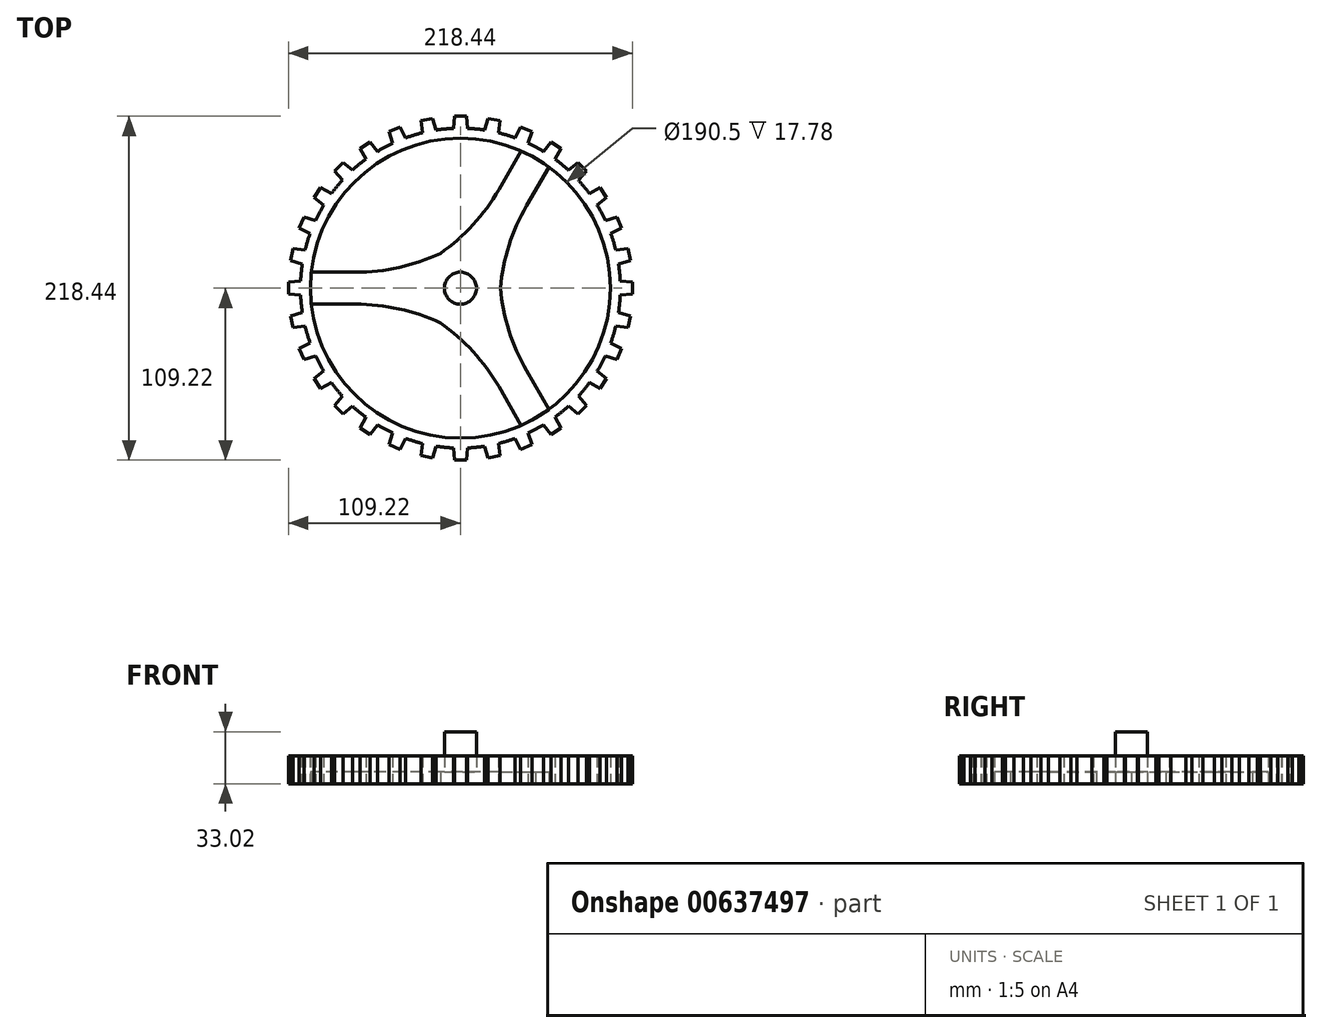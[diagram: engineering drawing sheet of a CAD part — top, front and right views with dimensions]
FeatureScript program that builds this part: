
annotation { "Feature Type Name" : "Feature", "Feature Type Description" : "" }
export const myFeature = defineFeature(function(context is Context, id is Id, definition is map)
    precondition{}
    {
        {
            var Q0;
            Q0=qCreatedBy(makeId("Top.planeOp"),FACE);
            var sketch = newSketch(context, id + "F0", { "sketchPlane" : qUnion([Q0])});
            skCircle(sketch, "E0", {"center": v(0, 0) * mm, "radius": 10.16 * mm});
            skCircle(sketch, "E1", {"center": v(0, 0) * mm, "radius": 12.7 * mm});
            skCircle(sketch, "E2", {"center": v(0, 0) * mm, "radius": 95.25 * mm});
            skCircle(sketch, "E3", {"center": v(0, 0) * mm, "radius": 101.6 * mm});
            skLineSegment(sketch, "E4", {"start": v(109.22, -3.81) * mm, "end": v(109.22, 3.81) * mm});
            skLineSegment(sketch, "E5", {"start": v(109.22, 3.81) * mm, "end": v(0, 12.7) * mm});
            skLineSegment(sketch, "E6", {"start": v(0, 12.7) * mm, "end": v(0, -12.7) * mm});
            skLineSegment(sketch, "E7", {"start": v(0, -12.7) * mm, "end": v(109.22, -3.81) * mm});
            skLineSegment(sketch, "E8", {"start": v(0, 0) * mm, "end": v(109.22, 0) * mm});
            skLineSegment(sketch, "E9.1.0", {"start": v(107.86, 17.57) * mm, "end": v(106.38, 25.04) * mm});
            skLineSegment(sketch, "E9.1.1", {"start": v(2.48, -12.46) * mm, "end": v(107.86, 17.57) * mm});
            skLineSegment(sketch, "E9.1.2", {"start": v(106.38, 25.04) * mm, "end": v(-2.48, 12.46) * mm});
            skLineSegment(sketch, "E9.2.0", {"start": v(102.36, 38.28) * mm, "end": v(99.45, 45.32) * mm});
            skLineSegment(sketch, "E9.2.1", {"start": v(4.86, -11.73) * mm, "end": v(102.36, 38.28) * mm});
            skLineSegment(sketch, "E9.2.2", {"start": v(99.45, 45.32) * mm, "end": v(-4.86, 11.73) * mm});
            skLineSegment(sketch, "E9.3.0", {"start": v(92.93, 57.51) * mm, "end": v(88.7, 63.85) * mm});
            skLineSegment(sketch, "E9.3.1", {"start": v(7.06, -10.56) * mm, "end": v(92.93, 57.51) * mm});
            skLineSegment(sketch, "E9.3.2", {"start": v(88.7, 63.85) * mm, "end": v(-7.06, 10.56) * mm});
            skLineSegment(sketch, "E9.4.0", {"start": v(79.92, 74.54) * mm, "end": v(74.54, 79.92) * mm});
            skLineSegment(sketch, "E9.4.1", {"start": v(8.98, -8.98) * mm, "end": v(79.92, 74.54) * mm});
            skLineSegment(sketch, "E9.4.2", {"start": v(74.54, 79.92) * mm, "end": v(-8.98, 8.98) * mm});
            skLineSegment(sketch, "E9.5.0", {"start": v(63.85, 88.7) * mm, "end": v(57.51, 92.93) * mm});
            skLineSegment(sketch, "E9.5.1", {"start": v(10.56, -7.06) * mm, "end": v(63.85, 88.7) * mm});
            skLineSegment(sketch, "E9.5.2", {"start": v(57.51, 92.93) * mm, "end": v(-10.56, 7.06) * mm});
            skLineSegment(sketch, "E9.6.0", {"start": v(45.32, 99.45) * mm, "end": v(38.28, 102.36) * mm});
            skLineSegment(sketch, "E9.6.1", {"start": v(11.73, -4.86) * mm, "end": v(45.32, 99.45) * mm});
            skLineSegment(sketch, "E9.6.2", {"start": v(38.28, 102.36) * mm, "end": v(-11.73, 4.86) * mm});
            skLineSegment(sketch, "E9.7.0", {"start": v(25.04, 106.38) * mm, "end": v(17.57, 107.86) * mm});
            skLineSegment(sketch, "E9.7.1", {"start": v(12.46, -2.48) * mm, "end": v(25.04, 106.38) * mm});
            skLineSegment(sketch, "E9.7.2", {"start": v(17.57, 107.86) * mm, "end": v(-12.46, 2.48) * mm});
            skLineSegment(sketch, "E9.8.0", {"start": v(3.81, 109.22) * mm, "end": v(-3.8, 109.22) * mm});
            skLineSegment(sketch, "E9.8.1", {"start": v(12.7, 0) * mm, "end": v(3.81, 109.22) * mm});
            skLineSegment(sketch, "E9.8.2", {"start": v(-3.8, 109.22) * mm, "end": v(-12.7, 0) * mm});
            skLineSegment(sketch, "E9.9.0", {"start": v(-17.57, 107.86) * mm, "end": v(-25.04, 106.38) * mm});
            skLineSegment(sketch, "E9.9.1", {"start": v(12.46, 2.48) * mm, "end": v(-17.57, 107.86) * mm});
            skLineSegment(sketch, "E9.9.2", {"start": v(-25.04, 106.38) * mm, "end": v(-12.46, -2.48) * mm});
            skLineSegment(sketch, "E9.10.0", {"start": v(-38.28, 102.36) * mm, "end": v(-45.32, 99.45) * mm});
            skLineSegment(sketch, "E9.10.1", {"start": v(11.73, 4.86) * mm, "end": v(-38.28, 102.36) * mm});
            skLineSegment(sketch, "E9.10.2", {"start": v(-45.32, 99.45) * mm, "end": v(-11.73, -4.86) * mm});
            skLineSegment(sketch, "E9.11.0", {"start": v(-57.51, 92.93) * mm, "end": v(-63.85, 88.7) * mm});
            skLineSegment(sketch, "E9.11.1", {"start": v(10.56, 7.06) * mm, "end": v(-57.51, 92.93) * mm});
            skLineSegment(sketch, "E9.11.2", {"start": v(-63.85, 88.7) * mm, "end": v(-10.56, -7.06) * mm});
            skLineSegment(sketch, "E9.12.0", {"start": v(-74.54, 79.92) * mm, "end": v(-79.92, 74.54) * mm});
            skLineSegment(sketch, "E9.12.1", {"start": v(8.98, 8.98) * mm, "end": v(-74.54, 79.92) * mm});
            skLineSegment(sketch, "E9.12.2", {"start": v(-79.92, 74.54) * mm, "end": v(-8.98, -8.98) * mm});
            skLineSegment(sketch, "E9.13.0", {"start": v(-88.7, 63.85) * mm, "end": v(-92.93, 57.51) * mm});
            skLineSegment(sketch, "E9.13.1", {"start": v(7.06, 10.56) * mm, "end": v(-88.7, 63.85) * mm});
            skLineSegment(sketch, "E9.13.2", {"start": v(-92.93, 57.51) * mm, "end": v(-7.06, -10.56) * mm});
            skLineSegment(sketch, "E9.14.0", {"start": v(-99.45, 45.32) * mm, "end": v(-102.36, 38.28) * mm});
            skLineSegment(sketch, "E9.14.1", {"start": v(4.86, 11.73) * mm, "end": v(-99.45, 45.32) * mm});
            skLineSegment(sketch, "E9.14.2", {"start": v(-102.36, 38.28) * mm, "end": v(-4.86, -11.73) * mm});
            skLineSegment(sketch, "E9.15.0", {"start": v(-106.38, 25.04) * mm, "end": v(-107.86, 17.57) * mm});
            skLineSegment(sketch, "E9.15.1", {"start": v(2.48, 12.46) * mm, "end": v(-106.38, 25.04) * mm});
            skLineSegment(sketch, "E9.15.2", {"start": v(-107.86, 17.57) * mm, "end": v(-2.48, -12.46) * mm});
            skLineSegment(sketch, "E9.16.0", {"start": v(-109.22, 3.81) * mm, "end": v(-109.22, -3.8) * mm});
            skLineSegment(sketch, "E9.16.1", {"start": v(0, 12.7) * mm, "end": v(-109.22, 3.81) * mm});
            skLineSegment(sketch, "E9.16.2", {"start": v(-109.22, -3.8) * mm, "end": v(0, -12.7) * mm});
            skLineSegment(sketch, "E9.17.0", {"start": v(-107.86, -17.57) * mm, "end": v(-106.38, -25.04) * mm});
            skLineSegment(sketch, "E9.17.1", {"start": v(-2.48, 12.46) * mm, "end": v(-107.86, -17.57) * mm});
            skLineSegment(sketch, "E9.17.2", {"start": v(-106.38, -25.04) * mm, "end": v(2.48, -12.46) * mm});
            skLineSegment(sketch, "E9.18.0", {"start": v(-102.36, -38.28) * mm, "end": v(-99.45, -45.32) * mm});
            skLineSegment(sketch, "E9.18.1", {"start": v(-4.86, 11.73) * mm, "end": v(-102.36, -38.28) * mm});
            skLineSegment(sketch, "E9.18.2", {"start": v(-99.45, -45.32) * mm, "end": v(4.86, -11.73) * mm});
            skLineSegment(sketch, "E9.19.0", {"start": v(-92.93, -57.51) * mm, "end": v(-88.7, -63.85) * mm});
            skLineSegment(sketch, "E9.19.1", {"start": v(-7.06, 10.56) * mm, "end": v(-92.93, -57.51) * mm});
            skLineSegment(sketch, "E9.19.2", {"start": v(-88.7, -63.85) * mm, "end": v(7.06, -10.56) * mm});
            skLineSegment(sketch, "E9.20.0", {"start": v(-79.92, -74.54) * mm, "end": v(-74.54, -79.92) * mm});
            skLineSegment(sketch, "E9.20.1", {"start": v(-8.98, 8.98) * mm, "end": v(-79.92, -74.54) * mm});
            skLineSegment(sketch, "E9.20.2", {"start": v(-74.54, -79.92) * mm, "end": v(8.98, -8.98) * mm});
            skLineSegment(sketch, "E9.21.0", {"start": v(-63.85, -88.7) * mm, "end": v(-57.51, -92.93) * mm});
            skLineSegment(sketch, "E9.21.1", {"start": v(-10.56, 7.06) * mm, "end": v(-63.85, -88.7) * mm});
            skLineSegment(sketch, "E9.21.2", {"start": v(-57.51, -92.93) * mm, "end": v(10.56, -7.06) * mm});
            skLineSegment(sketch, "E9.22.0", {"start": v(-45.32, -99.45) * mm, "end": v(-38.28, -102.36) * mm});
            skLineSegment(sketch, "E9.22.1", {"start": v(-11.73, 4.86) * mm, "end": v(-45.32, -99.45) * mm});
            skLineSegment(sketch, "E9.22.2", {"start": v(-38.28, -102.36) * mm, "end": v(11.73, -4.86) * mm});
            skLineSegment(sketch, "E9.23.0", {"start": v(-25.04, -106.38) * mm, "end": v(-17.57, -107.86) * mm});
            skLineSegment(sketch, "E9.23.1", {"start": v(-12.46, 2.48) * mm, "end": v(-25.04, -106.38) * mm});
            skLineSegment(sketch, "E9.23.2", {"start": v(-17.57, -107.86) * mm, "end": v(12.46, -2.48) * mm});
            skLineSegment(sketch, "E9.24.0", {"start": v(-3.81, -109.22) * mm, "end": v(3.8, -109.22) * mm});
            skLineSegment(sketch, "E9.24.1", {"start": v(-12.7, 0) * mm, "end": v(-3.81, -109.22) * mm});
            skLineSegment(sketch, "E9.24.2", {"start": v(3.8, -109.22) * mm, "end": v(12.7, 0) * mm});
            skLineSegment(sketch, "E9.25.0", {"start": v(17.57, -107.86) * mm, "end": v(25.04, -106.38) * mm});
            skLineSegment(sketch, "E9.25.1", {"start": v(-12.46, -2.48) * mm, "end": v(17.57, -107.86) * mm});
            skLineSegment(sketch, "E9.25.2", {"start": v(25.04, -106.38) * mm, "end": v(12.46, 2.48) * mm});
            skLineSegment(sketch, "E9.26.0", {"start": v(38.28, -102.36) * mm, "end": v(45.32, -99.45) * mm});
            skLineSegment(sketch, "E9.26.1", {"start": v(-11.73, -4.86) * mm, "end": v(38.28, -102.36) * mm});
            skLineSegment(sketch, "E9.26.2", {"start": v(45.32, -99.45) * mm, "end": v(11.73, 4.86) * mm});
            skLineSegment(sketch, "E9.27.0", {"start": v(57.51, -92.93) * mm, "end": v(63.85, -88.7) * mm});
            skLineSegment(sketch, "E9.27.1", {"start": v(-10.56, -7.06) * mm, "end": v(57.51, -92.93) * mm});
            skLineSegment(sketch, "E9.27.2", {"start": v(63.85, -88.7) * mm, "end": v(10.56, 7.06) * mm});
            skLineSegment(sketch, "E9.28.0", {"start": v(74.54, -79.92) * mm, "end": v(79.92, -74.54) * mm});
            skLineSegment(sketch, "E9.28.1", {"start": v(-8.98, -8.98) * mm, "end": v(74.54, -79.92) * mm});
            skLineSegment(sketch, "E9.28.2", {"start": v(79.92, -74.54) * mm, "end": v(8.98, 8.98) * mm});
            skLineSegment(sketch, "E9.29.0", {"start": v(88.7, -63.85) * mm, "end": v(92.93, -57.51) * mm});
            skLineSegment(sketch, "E9.29.1", {"start": v(-7.06, -10.56) * mm, "end": v(88.7, -63.85) * mm});
            skLineSegment(sketch, "E9.29.2", {"start": v(92.93, -57.51) * mm, "end": v(7.06, 10.56) * mm});
            skLineSegment(sketch, "E9.30.0", {"start": v(99.45, -45.32) * mm, "end": v(102.36, -38.28) * mm});
            skLineSegment(sketch, "E9.30.1", {"start": v(-4.86, -11.73) * mm, "end": v(99.45, -45.32) * mm});
            skLineSegment(sketch, "E9.30.2", {"start": v(102.36, -38.28) * mm, "end": v(4.86, 11.73) * mm});
            skLineSegment(sketch, "E9.31.0", {"start": v(106.38, -25.04) * mm, "end": v(107.86, -17.57) * mm});
            skLineSegment(sketch, "E9.31.1", {"start": v(-2.48, -12.46) * mm, "end": v(106.38, -25.04) * mm});
            skLineSegment(sketch, "E9.31.2", {"start": v(107.86, -17.57) * mm, "end": v(2.48, 12.46) * mm});
            skSolve(sketch);
        }
        {
            var Q0;
            Q0 = qSketchRegion(id + "F0", true);
            extrude(context, id + "F1", {"entities" : qUnion([Q0]), "depth" : 17.78 * mm, "offsetDistance" : 25.4 * mm});
        }
        {
            var Q0;
            Q0=makeQuery(id+"F1.opExtrude","CAP_FACE",FACE,{"disambiguationData":[OSD([sQuery(id+"F0.wireOp",EDGE,"E2"),sQuery(id+"F0.wireOp",EDGE,"E3"),sQuery(id+"F0.wireOp",EDGE,"E4"),sQuery(id+"F0.wireOp",EDGE,"E5"),sQuery(id+"F0.wireOp",EDGE,"E7"),sQuery(id+"F0.wireOp",EDGE,"E9.1.0"),sQuery(id+"F0.wireOp",EDGE,"E9.1.1"),sQuery(id+"F0.wireOp",EDGE,"E9.1.2"),sQuery(id+"F0.wireOp",EDGE,"E9.2.0"),sQuery(id+"F0.wireOp",EDGE,"E9.2.1"),sQuery(id+"F0.wireOp",EDGE,"E9.2.2"),sQuery(id+"F0.wireOp",EDGE,"E9.3.0"),sQuery(id+"F0.wireOp",EDGE,"E9.3.1"),sQuery(id+"F0.wireOp",EDGE,"E9.3.2"),sQuery(id+"F0.wireOp",EDGE,"E9.4.0"),sQuery(id+"F0.wireOp",EDGE,"E9.4.1"),sQuery(id+"F0.wireOp",EDGE,"E9.4.2"),sQuery(id+"F0.wireOp",EDGE,"E9.5.0"),sQuery(id+"F0.wireOp",EDGE,"E9.5.1"),sQuery(id+"F0.wireOp",EDGE,"E9.5.2"),sQuery(id+"F0.wireOp",EDGE,"E9.6.0"),sQuery(id+"F0.wireOp",EDGE,"E9.6.1"),sQuery(id+"F0.wireOp",EDGE,"E9.6.2"),sQuery(id+"F0.wireOp",EDGE,"E9.7.0"),sQuery(id+"F0.wireOp",EDGE,"E9.7.1"),sQuery(id+"F0.wireOp",EDGE,"E9.7.2"),sQuery(id+"F0.wireOp",EDGE,"E9.8.0"),sQuery(id+"F0.wireOp",EDGE,"E9.8.1"),sQuery(id+"F0.wireOp",EDGE,"E9.8.2"),sQuery(id+"F0.wireOp",EDGE,"E9.9.0"),sQuery(id+"F0.wireOp",EDGE,"E9.9.1"),sQuery(id+"F0.wireOp",EDGE,"E9.9.2"),sQuery(id+"F0.wireOp",EDGE,"E9.10.0"),sQuery(id+"F0.wireOp",EDGE,"E9.10.1"),sQuery(id+"F0.wireOp",EDGE,"E9.10.2"),sQuery(id+"F0.wireOp",EDGE,"E9.11.0"),sQuery(id+"F0.wireOp",EDGE,"E9.11.1"),sQuery(id+"F0.wireOp",EDGE,"E9.11.2"),sQuery(id+"F0.wireOp",EDGE,"E9.12.0"),sQuery(id+"F0.wireOp",EDGE,"E9.12.1"),sQuery(id+"F0.wireOp",EDGE,"E9.12.2"),sQuery(id+"F0.wireOp",EDGE,"E9.13.0"),sQuery(id+"F0.wireOp",EDGE,"E9.13.1"),sQuery(id+"F0.wireOp",EDGE,"E9.13.2"),sQuery(id+"F0.wireOp",EDGE,"E9.14.0"),sQuery(id+"F0.wireOp",EDGE,"E9.14.1"),sQuery(id+"F0.wireOp",EDGE,"E9.14.2"),sQuery(id+"F0.wireOp",EDGE,"E9.15.0"),sQuery(id+"F0.wireOp",EDGE,"E9.15.1"),sQuery(id+"F0.wireOp",EDGE,"E9.15.2"),sQuery(id+"F0.wireOp",EDGE,"E9.16.0"),sQuery(id+"F0.wireOp",EDGE,"E9.16.1"),sQuery(id+"F0.wireOp",EDGE,"E9.16.2"),sQuery(id+"F0.wireOp",EDGE,"E9.17.0"),sQuery(id+"F0.wireOp",EDGE,"E9.17.1"),sQuery(id+"F0.wireOp",EDGE,"E9.17.2"),sQuery(id+"F0.wireOp",EDGE,"E9.18.0"),sQuery(id+"F0.wireOp",EDGE,"E9.18.1"),sQuery(id+"F0.wireOp",EDGE,"E9.18.2"),sQuery(id+"F0.wireOp",EDGE,"E9.19.0"),sQuery(id+"F0.wireOp",EDGE,"E9.19.1"),sQuery(id+"F0.wireOp",EDGE,"E9.19.2"),sQuery(id+"F0.wireOp",EDGE,"E9.20.0"),sQuery(id+"F0.wireOp",EDGE,"E9.20.1"),sQuery(id+"F0.wireOp",EDGE,"E9.20.2"),sQuery(id+"F0.wireOp",EDGE,"E9.21.0"),sQuery(id+"F0.wireOp",EDGE,"E9.21.1"),sQuery(id+"F0.wireOp",EDGE,"E9.21.2"),sQuery(id+"F0.wireOp",EDGE,"E9.22.0"),sQuery(id+"F0.wireOp",EDGE,"E9.22.1"),sQuery(id+"F0.wireOp",EDGE,"E9.22.2"),sQuery(id+"F0.wireOp",EDGE,"E9.23.0"),sQuery(id+"F0.wireOp",EDGE,"E9.23.1"),sQuery(id+"F0.wireOp",EDGE,"E9.23.2"),sQuery(id+"F0.wireOp",EDGE,"E9.24.0"),sQuery(id+"F0.wireOp",EDGE,"E9.24.1"),sQuery(id+"F0.wireOp",EDGE,"E9.24.2"),sQuery(id+"F0.wireOp",EDGE,"E9.25.0"),sQuery(id+"F0.wireOp",EDGE,"E9.25.1"),sQuery(id+"F0.wireOp",EDGE,"E9.25.2"),sQuery(id+"F0.wireOp",EDGE,"E9.26.0"),sQuery(id+"F0.wireOp",EDGE,"E9.26.1"),sQuery(id+"F0.wireOp",EDGE,"E9.26.2"),sQuery(id+"F0.wireOp",EDGE,"E9.27.0"),sQuery(id+"F0.wireOp",EDGE,"E9.27.1"),sQuery(id+"F0.wireOp",EDGE,"E9.27.2"),sQuery(id+"F0.wireOp",EDGE,"E9.28.0"),sQuery(id+"F0.wireOp",EDGE,"E9.28.1"),sQuery(id+"F0.wireOp",EDGE,"E9.28.2"),sQuery(id+"F0.wireOp",EDGE,"E9.29.0"),sQuery(id+"F0.wireOp",EDGE,"E9.29.1"),sQuery(id+"F0.wireOp",EDGE,"E9.29.2"),sQuery(id+"F0.wireOp",EDGE,"E9.30.0"),sQuery(id+"F0.wireOp",EDGE,"E9.30.1"),sQuery(id+"F0.wireOp",EDGE,"E9.30.2"),sQuery(id+"F0.wireOp",EDGE,"E9.31.0"),sQuery(id+"F0.wireOp",EDGE,"E9.31.1"),sQuery(id+"F0.wireOp",EDGE,"E9.31.2")])],"isStart":true});
            var sketch = newSketch(context, id + "F2", { "sketchPlane" : qUnion([Q0])});
            skCircle(sketch, "E10", {"center": v(0, 0) * mm, "radius": 10.16 * mm});
            skCircle(sketch, "E11", {"center": v(0, 0) * mm, "radius": 25.4 * mm});
            skLineSegment(sketch, "E12", {"start": v(0, 0) * mm, "end": v(0, 10.16) * mm});
            skLineSegment(sketch, "E13", {"start": v(0, 0) * mm, "end": v(0, -10.16) * mm});
            skLineSegment(sketch, "E14", {"start": v(0, -10.16) * mm, "end": v(-94.7, -10.16) * mm});
            skLineSegment(sketch, "E15", {"start": v(0, 10.16) * mm, "end": v(-94.7, 10.16) * mm});
            skLineSegment(sketch, "E16", {"start": v(-94.7, 10.16) * mm, "end": v(-95.25, 0) * mm});
            skLineSegment(sketch, "E17", {"start": v(-95.25, 0) * mm, "end": v(-94.7, -10.16) * mm});
            skArc(sketch, "E18", {"start": v(-11.07, -22.86) * mm, "mid": v(-38.03, -13.38) * mm, "end": v(-66.43, -10.16) * mm});
            skArc(sketch, "E19.MirrorCS", {"start": v(-11.07, 22.86) * mm, "mid": v(-38.03, 13.38) * mm, "end": v(-66.43, 10.16) * mm});
            skArc(sketch, "E20.1.0", {"start": v(25.33, 1.84) * mm, "mid": v(30.6, -26.25) * mm, "end": v(42.01, -52.45) * mm});
            skLineSegment(sketch, "E20.1.1", {"start": v(8.8, 5.08) * mm, "end": v(56.15, -76.94) * mm});
            skLineSegment(sketch, "E20.1.2", {"start": v(-8.8, -5.08) * mm, "end": v(38.55, -87.1) * mm});
            skArc(sketch, "E20.1.3", {"start": v(-14.26, -21.02) * mm, "mid": v(7.43, -39.62) * mm, "end": v(24.42, -62.6) * mm});
            skLineSegment(sketch, "E20.1.4", {"start": v(47.62, -82.49) * mm, "end": v(56.15, -76.94) * mm});
            skLineSegment(sketch, "E20.1.5", {"start": v(38.55, -87.1) * mm, "end": v(47.62, -82.49) * mm});
            skArc(sketch, "E20.2.0", {"start": v(-14.26, 21.02) * mm, "mid": v(7.43, 39.62) * mm, "end": v(24.42, 62.6) * mm});
            skLineSegment(sketch, "E20.2.1", {"start": v(-8.8, 5.08) * mm, "end": v(38.55, 87.1) * mm});
            skLineSegment(sketch, "E20.2.2", {"start": v(8.8, -5.08) * mm, "end": v(56.15, 76.94) * mm});
            skArc(sketch, "E20.2.3", {"start": v(25.33, -1.84) * mm, "mid": v(30.6, 26.25) * mm, "end": v(42.01, 52.45) * mm});
            skLineSegment(sketch, "E20.2.4", {"start": v(47.63, 82.49) * mm, "end": v(38.55, 87.1) * mm});
            skLineSegment(sketch, "E20.2.5", {"start": v(56.15, 76.94) * mm, "end": v(47.63, 82.49) * mm});
            skSolve(sketch);
        }
        {
            var Q0;
            Q0 = qSketchRegion(id + "F2", true);
            var Q1;
            {var subQ3=sQuery(id+"F2.wireOp",EDGE,"E20.2.2");var subQ9=sQuery(id+"F2.wireOp",EDGE,"E11");var subQ10=makeQuery(id+"F2.imprint","INTERSECT",VERTEX,{"derivedFrom":[subQ9,subQ3]});Q1=makeQuery(id+"F2.imprint","IMPRINT",FACE,{"disambiguationData":[TD([[makeQuery(id+"F2.imprint","IMPRINT",EDGE,{"disambiguationData":[TD([[subQ10,-1.0]])],"derivedFrom":subQ9}),1.0]])]});}
            var Q2;
            {var subQ1=sQuery(id+"F2.wireOp",EDGE,"E11");var subQ6=makeQuery(id+"F2.imprint","INTERSECT",VERTEX,{"derivedFrom":[subQ1,sQuery(id+"F2.wireOp",EDGE,"E19.MirrorCS")]});Q2=makeQuery(id+"F2.imprint","IMPRINT",FACE,{"disambiguationData":[TD([[makeQuery(id+"F2.imprint","IMPRINT",EDGE,{"disambiguationData":[TD([[subQ6,1.0]])],"derivedFrom":subQ1}),1.0]])]});}
            var Q3;
            {var subQ7=sQuery(id+"F2.wireOp",EDGE,"E20.1.2");var subQ9=sQuery(id+"F2.wireOp",EDGE,"E10");var subQ10=makeQuery(id+"F2.imprint","INTERSECT",VERTEX,{"derivedFrom":[subQ9,subQ7]});Q3=makeQuery(id+"F2.imprint","IMPRINT",FACE,{"disambiguationData":[TD([[makeQuery(id+"F2.imprint","IMPRINT",EDGE,{"disambiguationData":[TD([[subQ10,1.0]])],"derivedFrom":subQ9}),-1.0]])]});}
            var Q4;
            {var subQ1=sQuery(id+"F2.wireOp",EDGE,"E11");var subQ7=makeQuery(id+"F2.imprint","INTERSECT",VERTEX,{"derivedFrom":[subQ1,sQuery(id+"F2.wireOp",EDGE,"E20.1.3")]});Q4=makeQuery(id+"F2.imprint","IMPRINT",FACE,{"disambiguationData":[TD([[makeQuery(id+"F2.imprint","IMPRINT",EDGE,{"disambiguationData":[TD([[subQ7,1.0]])],"derivedFrom":subQ1}),1.0]])]});}
            var Q5;
            {var subQ1=sQuery(id+"F2.wireOp",EDGE,"E11");var subQ5=sQuery(id+"F2.wireOp",EDGE,"E20.1.2");var subQ6=makeQuery(id+"F2.imprint","INTERSECT",VERTEX,{"derivedFrom":[subQ1,subQ5]});Q5=makeQuery(id+"F2.imprint","IMPRINT",FACE,{"disambiguationData":[TD([[makeQuery(id+"F2.imprint","IMPRINT",EDGE,{"disambiguationData":[TD([[subQ6,-1.0]])],"derivedFrom":subQ1}),1.0]])]});}
            var Q6;
            {var subQ1=sQuery(id+"F2.wireOp",EDGE,"E11");var subQ5=makeQuery(id+"F2.imprint","INTERSECT",VERTEX,{"derivedFrom":[subQ1,sQuery(id+"F2.wireOp",EDGE,"E20.1.0")]});Q6=makeQuery(id+"F2.imprint","IMPRINT",FACE,{"disambiguationData":[TD([[makeQuery(id+"F2.imprint","IMPRINT",EDGE,{"disambiguationData":[TD([[subQ5,-1.0]])],"derivedFrom":subQ1}),1.0]])]});}
            var Q7;
            {var subQ1=sQuery(id+"F2.wireOp",EDGE,"E10");var subQ3=sQuery(id+"F2.wireOp",EDGE,"E20.2.1");var subQ4=makeQuery(id+"F2.imprint","INTERSECT",VERTEX,{"derivedFrom":[subQ1,subQ3]});Q7=makeQuery(id+"F2.imprint","IMPRINT",FACE,{"disambiguationData":[TD([[makeQuery(id+"F2.imprint","IMPRINT",EDGE,{"disambiguationData":[TD([[subQ4,-1.0]])],"derivedFrom":subQ3}),-1.0]])]});}
            var Q8;
            {var subQ1=sQuery(id+"F2.wireOp",EDGE,"E10");var subQ3=sQuery(id+"F2.wireOp",EDGE,"E20.1.2");var subQ4=makeQuery(id+"F2.imprint","INTERSECT",VERTEX,{"derivedFrom":[subQ1,subQ3]});Q8=makeQuery(id+"F2.imprint","IMPRINT",FACE,{"disambiguationData":[TD([[makeQuery(id+"F2.imprint","IMPRINT",EDGE,{"disambiguationData":[TD([[subQ4,-1.0]])],"derivedFrom":subQ3}),1.0]])]});}
            var Q9;
            {var subQ0=sQuery(id+"F2.wireOp",EDGE,"E20.1.1");var subQ1=sQuery(id+"F2.wireOp",EDGE,"E10");var subQ2=makeQuery(id+"F2.imprint","INTERSECT",VERTEX,{"derivedFrom":[subQ1,subQ0]});Q9=makeQuery(id+"F2.imprint","IMPRINT",FACE,{"disambiguationData":[TD([[makeQuery(id+"F2.imprint","IMPRINT",EDGE,{"disambiguationData":[TD([[subQ2,1.0]])],"derivedFrom":subQ1}),-1.0]])]});}
            var Q10;
            {var subQ0=sQuery(id+"F2.wireOp",EDGE,"E12");Q10=makeQuery(id+"F2.imprint","IMPRINT",FACE,{"disambiguationData":[TD([[makeQuery(id+"F2.imprint","IMPRINT",EDGE,{"derivedFrom":subQ0}),-1.0]])]});}
            var Q11;
            {var subQ0=sQuery(id+"F2.wireOp",EDGE,"E12");Q11=makeQuery(id+"F2.imprint","IMPRINT",FACE,{"disambiguationData":[TD([[makeQuery(id+"F2.imprint","IMPRINT",EDGE,{"derivedFrom":subQ0}),1.0]])]});}
            extrude(context, id + "F3", {"entities" : qUnion([Q0, Q1, Q2, Q3, Q4, Q5, Q6, Q7, Q8, Q9, Q10, Q11]), "oppositeDirection" : true, "depth" : 7.62 * mm, "offsetDistance" : 25.4 * mm});
        }
        {
            var Q0;
            {var subQ0=sQuery(id+"F2.wireOp",EDGE,"E12");Q0=makeQuery(id+"F2.imprint","IMPRINT",FACE,{"disambiguationData":[TD([[makeQuery(id+"F2.imprint","IMPRINT",EDGE,{"derivedFrom":subQ0}),1.0]])]});}
            var Q1;
            {var subQ0=sQuery(id+"F2.wireOp",EDGE,"E12");Q1=makeQuery(id+"F2.imprint","IMPRINT",FACE,{"disambiguationData":[TD([[makeQuery(id+"F2.imprint","IMPRINT",EDGE,{"derivedFrom":subQ0}),-1.0]])]});}
            extrude(context, id + "F4", {"entities" : qUnion([Q0, Q1]), "operationType" : NewBodyOperationType.ADD, "oppositeDirection" : true, "depth" : 33.02 * mm, "offsetDistance" : 25.4 * mm});
        }
    });
